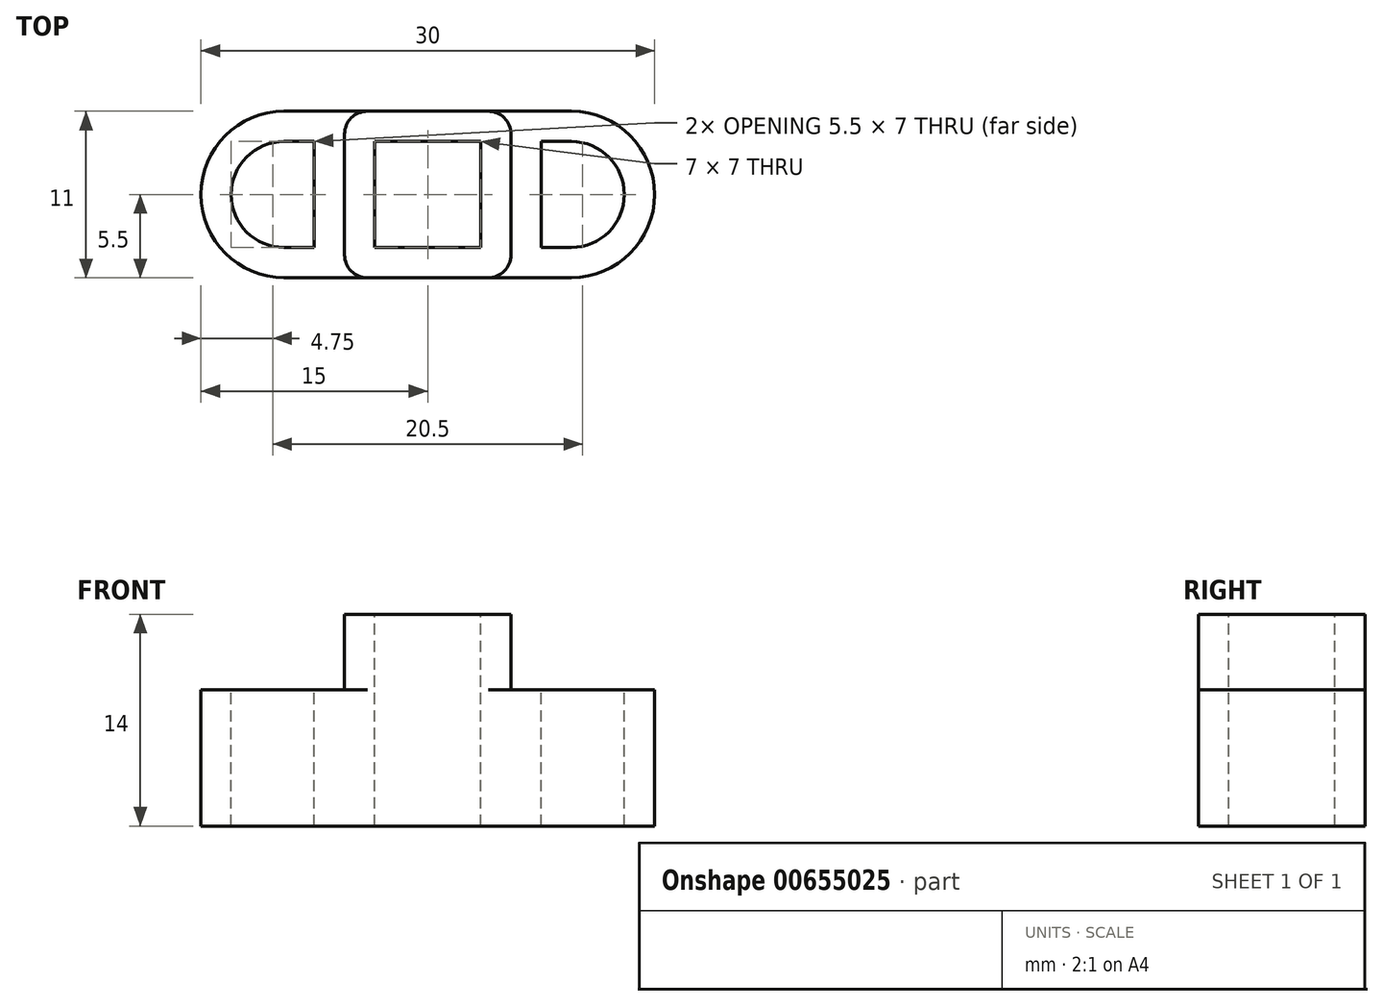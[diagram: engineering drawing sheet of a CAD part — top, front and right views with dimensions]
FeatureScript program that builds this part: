
annotation { "Feature Type Name" : "Feature", "Feature Type Description" : "" }
export const myFeature = defineFeature(function(context is Context, id is Id, definition is map)
    precondition{}
    {
        {
            var Q0;
            Q0=qCreatedBy(makeId("Top.planeOp"),FACE);
            var sketch = newSketch(context, id + "F0", { "sketchPlane" : qUnion([Q0])});
            skLineSegment(sketch, "E0.bottom", {"start": v(0, 0) * mm, "end": v(30, 0) * mm});
            skLineSegment(sketch, "E0.top", {"start": v(0, 11) * mm, "end": v(30, 11) * mm});
            skLineSegment(sketch, "E0.left", {"start": v(0, 0) * mm, "end": v(0, 11) * mm});
            skLineSegment(sketch, "E0.right", {"start": v(30, 0) * mm, "end": v(30, 11) * mm});
            skSolve(sketch);
        }
        {
            var Q0;
            Q0 = qSketchRegion(id + "F0", true);
            extrude(context, id + "F1", {"entities" : qUnion([Q0]), "depth" : 9 * mm, "offsetDistance" : 25 * mm});
        }
        {
            var Q0;
            Q0=makeQuery(id+"F1.opExtrude","CAP_FACE",FACE,{"disambiguationData":[OSD([sQuery(id+"F0.wireOp",EDGE,"E0.bottom"),sQuery(id+"F0.wireOp",EDGE,"E0.top"),sQuery(id+"F0.wireOp",EDGE,"E0.left"),sQuery(id+"F0.wireOp",EDGE,"E0.right")])],"isStart":false});
            var sketch = newSketch(context, id + "F2", { "sketchPlane" : qUnion([Q0])});
            skLineSegment(sketch, "E1.bottom", {"start": v(9.5, 11) * mm, "end": v(20.5, 11) * mm});
            skLineSegment(sketch, "E1.top", {"start": v(9.5, 0) * mm, "end": v(20.5, 0) * mm});
            skLineSegment(sketch, "E1.left", {"start": v(9.5, 11) * mm, "end": v(9.5, 0) * mm});
            skLineSegment(sketch, "E1.right", {"start": v(20.5, 11) * mm, "end": v(20.5, 0) * mm});
            skLineSegment(sketch, "E2", {"start": v(0, 11) * mm, "end": v(15, 11) * mm, "construction": true});
            skSolve(sketch);
        }
        {
            var Q0;
            Q0=makeQuery(id+"F2.imprint","IMPRINT",FACE,{"disambiguationData":[TD([[makeQuery(id+"F2.imprint","IMPRINT",EDGE,{"derivedFrom":sQuery(id+"F2.wireOp",EDGE,"E1.bottom")}),-1.0]])]});
            extrude(context, id + "F3", {"entities" : qUnion([Q0]), "operationType" : NewBodyOperationType.ADD, "depth" : 5 * mm, "offsetDistance" : 25 * mm});
        }
        {
            var Q0;
            Q0=makeQuery(id+"F3.opExtrude","SWEPT_EDGE",EDGE,{"disambiguationData":[OSD([sQuery(id+"F0.wireOp",EDGE,"E0.top"),sQuery(id+"F2.wireOp",EDGE,"E1.bottom"),sQuery(id+"F2.wireOp",EDGE,"E1.right")])]});
            var Q1;
            Q1=makeQuery(id+"F3.opExtrude","SWEPT_EDGE",EDGE,{"disambiguationData":[OSD([sQuery(id+"F0.wireOp",EDGE,"E0.top"),sQuery(id+"F2.wireOp",EDGE,"E1.bottom"),sQuery(id+"F2.wireOp",EDGE,"E1.left")])]});
            var Q2;
            Q2=makeQuery(id+"F3.opExtrude","SWEPT_EDGE",EDGE,{"disambiguationData":[OSD([sQuery(id+"F0.wireOp",EDGE,"E0.bottom"),sQuery(id+"F2.wireOp",EDGE,"E1.top"),sQuery(id+"F2.wireOp",EDGE,"E1.left")])]});
            var Q3;
            Q3=makeQuery(id+"F3.opExtrude","SWEPT_EDGE",EDGE,{"disambiguationData":[OSD([sQuery(id+"F0.wireOp",EDGE,"E0.bottom"),sQuery(id+"F2.wireOp",EDGE,"E1.top"),sQuery(id+"F2.wireOp",EDGE,"E1.right")])]});
            fillet(context, id + "F4", {"entities" : qUnion([Q0, Q1, Q2, Q3]), "radius" : 1.5 * mm, "tangentPropagation" : true, "allowEdgeOverflow" : false});
        }
        {
            var Q0;
            Q0=makeQuery(id+"F1.opExtrude","SWEPT_EDGE",EDGE,{"disambiguationData":[OSD([sQuery(id+"F0.wireOp",EDGE,"E0.top"),sQuery(id+"F0.wireOp",EDGE,"E0.right")])]});
            var Q1;
            Q1=makeQuery(id+"F1.opExtrude","SWEPT_EDGE",EDGE,{"disambiguationData":[OSD([sQuery(id+"F0.wireOp",EDGE,"E0.bottom"),sQuery(id+"F0.wireOp",EDGE,"E0.right")])]});
            var Q2;
            Q2=makeQuery(id+"F1.opExtrude","SWEPT_EDGE",EDGE,{"disambiguationData":[OSD([sQuery(id+"F0.wireOp",EDGE,"E0.top"),sQuery(id+"F0.wireOp",EDGE,"E0.left")])]});
            var Q3;
            Q3=makeQuery(id+"F1.opExtrude","SWEPT_EDGE",EDGE,{"disambiguationData":[OSD([sQuery(id+"F0.wireOp",EDGE,"E0.bottom"),sQuery(id+"F0.wireOp",EDGE,"E0.left")])]});
            fillet(context, id + "F5", {"entities" : qUnion([Q0, Q1, Q2, Q3]), "radius" : 5.5 * mm, "tangentPropagation" : true, "allowEdgeOverflow" : false});
        }
        {
            var Q0;
            Q0=makeQuery(id+"F3.opExtrude","CAP_FACE",FACE,{"disambiguationData":[OSD([sQuery(id+"F2.wireOp",EDGE,"E1.bottom"),sQuery(id+"F2.wireOp",EDGE,"E1.top"),sQuery(id+"F2.wireOp",EDGE,"E1.left"),sQuery(id+"F2.wireOp",EDGE,"E1.right")])],"isStart":false});
            var sketch = newSketch(context, id + "F6", { "sketchPlane" : qUnion([Q0])});
            skLineSegment(sketch, "E3.1", {"start": v(11.5, 2) * mm, "end": v(18.5, 2) * mm});
            skLineSegment(sketch, "E3.2", {"start": v(18.5, 2) * mm, "end": v(18.5, 9) * mm});
            skLineSegment(sketch, "E3.5", {"start": v(18.5, 9) * mm, "end": v(11.5, 9) * mm});
            skLineSegment(sketch, "E3.7", {"start": v(11.5, 9) * mm, "end": v(11.5, 2) * mm});
            skSolve(sketch);
        }
        {
            var Q0;
            Q0=makeQuery(id+"F6.imprint","IMPRINT",FACE,{"disambiguationData":[TD([[makeQuery(id+"F6.imprint","IMPRINT",EDGE,{"derivedFrom":sQuery(id+"F6.wireOp",EDGE,"E3.1")}),1.0]])]});
            extrude(context, id + "F7", {"entities" : qUnion([Q0]), "operationType" : NewBodyOperationType.REMOVE, "oppositeDirection" : true, "depth" : 25 * mm, "offsetDistance" : 25 * mm});
        }
        {
            var Q0;
            {var subQ0=sQuery(id+"F0.wireOp",EDGE,"E0.top");var subQ1=sQuery(id+"F0.wireOp",EDGE,"E0.right");var subQ2=sQuery(id+"F0.wireOp",EDGE,"E0.bottom");Q0=makeQuery(id+"F3.boolean.opBoolean","SPLIT",FACE,{"disambiguationData":[TD([makeQuery(id+"F1.opExtrude","SWEPT_FACE",FACE,{"disambiguationData":[OSD([subQ1])]})])],"derivedFrom":makeQuery(id+"F1.opExtrude","CAP_FACE",FACE,{"disambiguationData":[OSD([subQ2,subQ0,sQuery(id+"F0.wireOp",EDGE,"E0.left"),subQ1])],"isStart":false})});}
            var sketch = newSketch(context, id + "F8", { "sketchPlane" : qUnion([Q0])});
            skLineSegment(sketch, "E4", {"start": v(22.5, 9) * mm, "end": v(22.5, 2) * mm});
            skLineSegment(sketch, "E5", {"start": v(22.5, 2) * mm, "end": v(24.5, 2) * mm});
            skLineSegment(sketch, "E6", {"start": v(22.5, 9) * mm, "end": v(24.5, 9) * mm});
            skArc(sketch, "E7", {"start": v(24.5, 2) * mm, "mid": v(28, 5.5) * mm, "end": v(24.5, 9) * mm});
            skLineSegment(sketch, "E8", {"start": v(24.5, 9) * mm, "end": v(24.5, 2) * mm, "construction": true});
            skPoint(sketch, "E9.0", {"position": v(15, 9) * mm});
            skLineSegment(sketch, "E10", {"start": v(15, 9) * mm, "end": v(15, 2.18) * mm, "construction": true});
            skLineSegment(sketch, "E11.MirrorCS", {"start": v(7.5, 9) * mm, "end": v(7.5, 2) * mm});
            skLineSegment(sketch, "E12.MirrorCS", {"start": v(7.5, 2) * mm, "end": v(5.5, 2) * mm});
            skLineSegment(sketch, "E13.MirrorCS", {"start": v(7.5, 9) * mm, "end": v(5.5, 9) * mm});
            skArc(sketch, "E14.MirrorCS", {"start": v(5.5, 2) * mm, "mid": v(2, 5.5) * mm, "end": v(5.5, 9) * mm});
            skLineSegment(sketch, "E15.MirrorCS", {"start": v(5.5, 9) * mm, "end": v(5.5, 2) * mm, "construction": true});
            skSolve(sketch);
        }
        {
            var Q0;
            Q0 = qSketchRegion(id + "F8", true);
            extrude(context, id + "F9", {"entities" : qUnion([Q0]), "operationType" : NewBodyOperationType.REMOVE, "oppositeDirection" : true, "depth" : 25 * mm, "offsetDistance" : 25 * mm});
        }
    });
